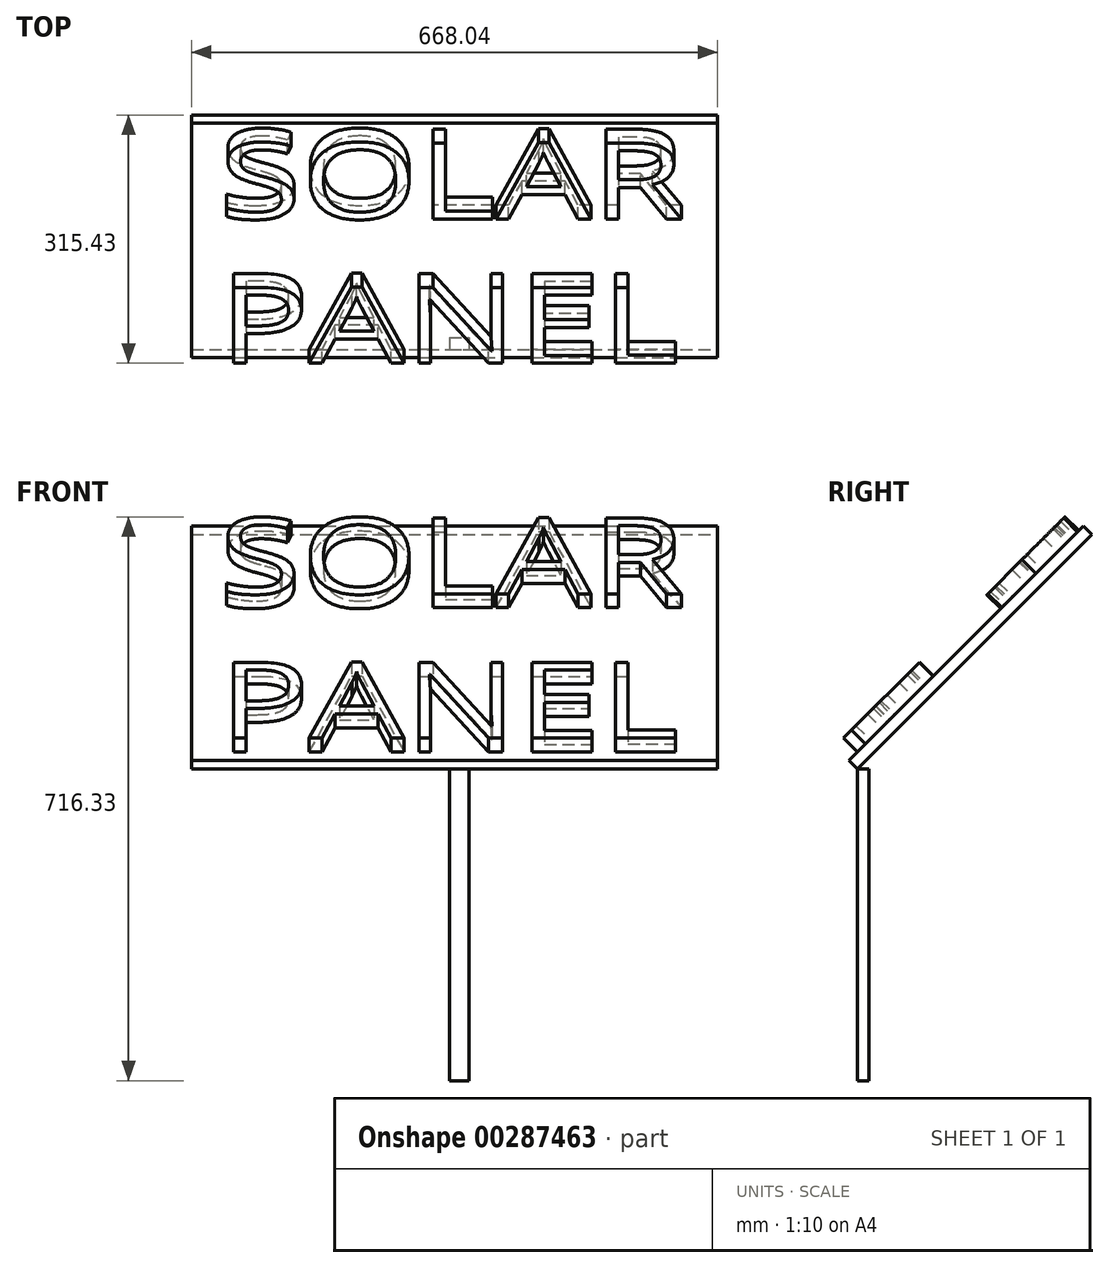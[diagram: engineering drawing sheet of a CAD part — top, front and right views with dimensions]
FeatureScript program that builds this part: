
annotation { "Feature Type Name" : "Feature", "Feature Type Description" : "" }
export const myFeature = defineFeature(function(context is Context, id is Id, definition is map)
    precondition{}
    {
        {
            var Q0;
            Q0=qCreatedBy(makeId("Front.planeOp"),FACE);
            var sketch = newSketch(context, id + "F0", { "sketchPlane" : qUnion([Q0])});
            skLineSegment(sketch, "E0.bottom", {"start": v(0, 0) * mm, "end": v(25, 0) * mm});
            skLineSegment(sketch, "E0.top", {"start": v(0, 396.13) * mm, "end": v(25, 396.13) * mm});
            skLineSegment(sketch, "E0.left", {"start": v(0, 0) * mm, "end": v(0, 396.13) * mm});
            skLineSegment(sketch, "E0.right", {"start": v(25, 0) * mm, "end": v(25, 396.13) * mm});
            skSolve(sketch);
        }
        {
            var Q0;
            Q0=qSketchRegion(id+"F0",true);
            extrude(context, id + "F1", {"entities" : qUnion([Q0]), "oppositeDirection" : true, "depth" : 15 * mm});
        }
        {
            var Q0;
            Q0=makeQuery(id+"F1.opExtrude","SWEPT_FACE",FACE,{"disambiguationData":[OSD([sQuery(id+"F0.wireOp",EDGE,"E0.top")])]});
            var sketch = newSketch(context, id + "F2", { "sketchPlane" : qUnion([Q0])});
            skLineSegment(sketch, "E1.bottom", {"start": v(-327.59, 421.17) * mm, "end": v(340.45, 421.17) * mm});
            skLineSegment(sketch, "E1.top", {"start": v(-327.59, 0) * mm, "end": v(340.45, 0) * mm});
            skLineSegment(sketch, "E1.left", {"start": v(-327.59, 421.17) * mm, "end": v(-327.59, 0) * mm});
            skLineSegment(sketch, "E1.right", {"start": v(340.45, 421.17) * mm, "end": v(340.45, 0) * mm});
            skSolve(sketch);
        }
        {
            var Q0;
            Q0=qSketchRegion(id+"F2",true);
            extrude(context, id + "F3", {"entities" : qUnion([Q0]), "depth" : 15 * mm});
        }
        {
            var Q0;
            Q0=makeQuery(id+"F3.opExtrude","CAP_FACE",FACE,{"disambiguationData":[OSD([sQuery(id+"F2.wireOp",EDGE,"E1.bottom"),sQuery(id+"F2.wireOp",EDGE,"E1.top"),sQuery(id+"F2.wireOp",EDGE,"E1.left"),sQuery(id+"F2.wireOp",EDGE,"E1.right")])],"isStart":false});
            var sketch = newSketch(context, id + "F4", { "sketchPlane" : qUnion([Q0])});
            skText(sketch, "E2", { "text": "SOLAR\nPANEL", "fontName": "OpenSans-Regular.ttf"});
            const initialGuessF4  = {"E2": [-0.29311, 0.2745, 1, 0, 0.13734]};
            skSetInitialGuess(sketch, initialGuessF4);
            skSolve(sketch);
        }
        {
            var Q0;
            Q0=qSketchRegion(id+"F4",true);
            extrude(context, id + "F5", {"entities" : qUnion([Q0]), "operationType" : NewBodyOperationType.ADD, "depth" : 25 * mm});
        }
        {
            var Q0;
            Q0=makeQuery(id+"F3.opExtrude","SWEPT_BODY",BODY,{"disambiguationData":[OSD([sQuery(id+"F2.wireOp",EDGE,"E1.bottom"),sQuery(id+"F2.wireOp",EDGE,"E1.top"),sQuery(id+"F2.wireOp",EDGE,"E1.left"),sQuery(id+"F2.wireOp",EDGE,"E1.right")])]});
            var Q1;
            Q1=makeQuery(id+"F3.opExtrude","CAP_EDGE",EDGE,{"disambiguationData":[OSD([sQuery(id+"F2.wireOp",EDGE,"E1.top")])],"isStart":true});
            transform(context, id + "F6", {"entities" : qUnion([Q0]), "transformType" : TransformType.ROTATION, "transformAxis" : qUnion([Q1]), "angle" : 45 * degree, "makeCopy" : false});
        }
    });
